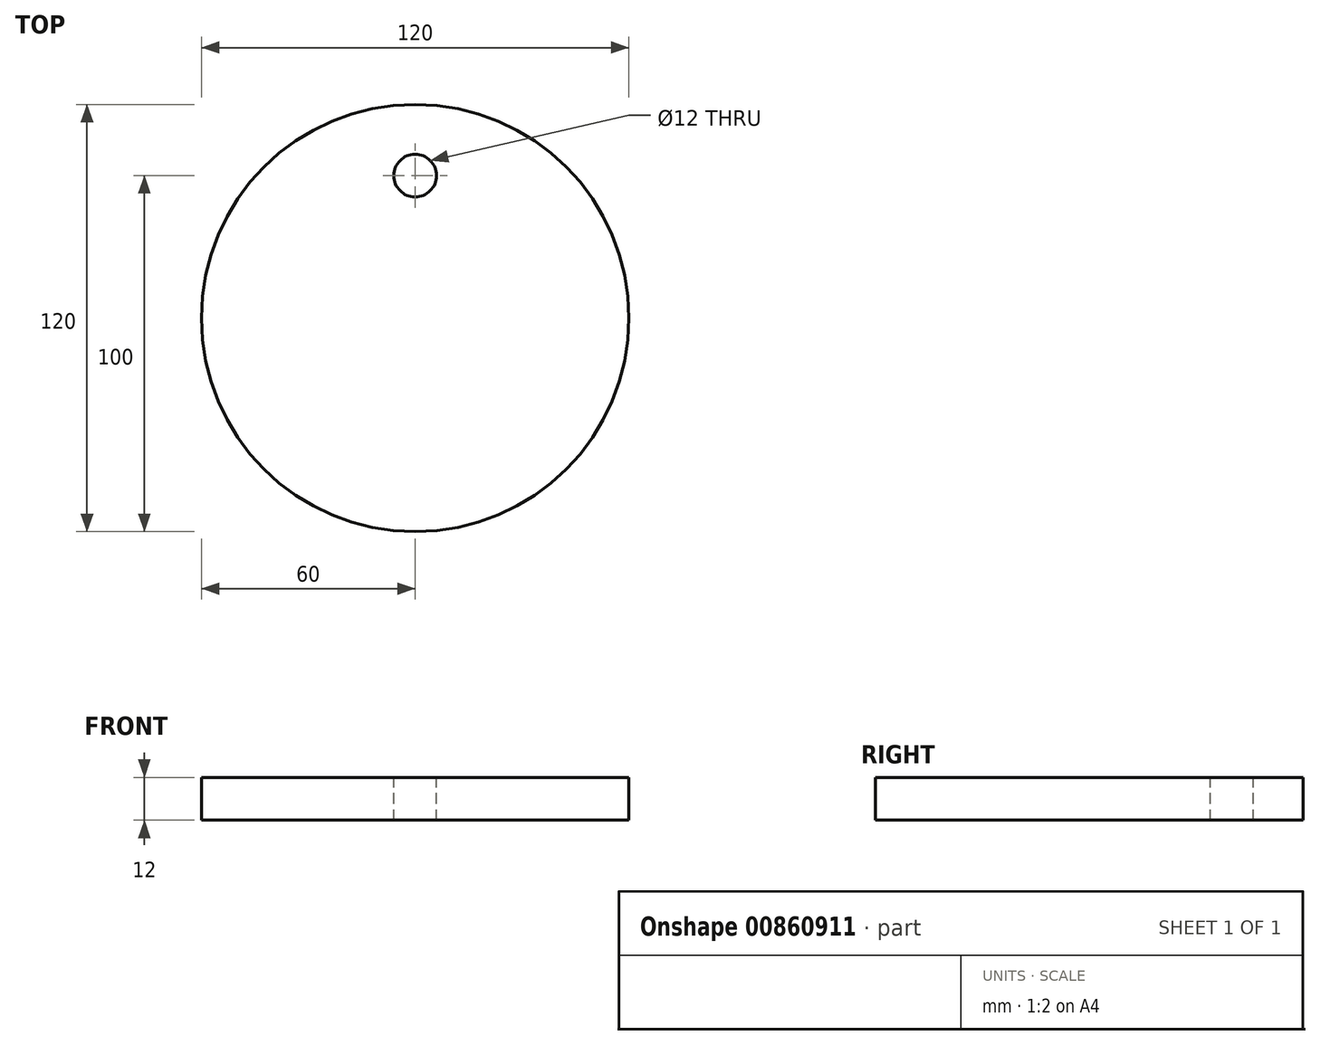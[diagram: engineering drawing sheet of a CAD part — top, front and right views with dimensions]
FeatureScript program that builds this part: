
annotation { "Feature Type Name" : "Feature", "Feature Type Description" : "" }
export const myFeature = defineFeature(function(context is Context, id is Id, definition is map)
    precondition{}
    {
        {
            assignVariable(context, id + "F0", {"name" : "BigCircle", "anyValue" : 120});
        }
        {
            assignVariable(context, id + "F1", {"name" : "Thickness", "anyValue" : getVariable(context, 'BigCircle') / 10});
        }
        {
            var Q0;
            Q0=qCreatedBy(makeId("Top.planeOp"),FACE);
            var sketch = newSketch(context, id + "F2", { "sketchPlane" : qUnion([Q0])});
            skCircle(sketch, "E0", {"center": v(0, 0) * mm, "radius": 60 * mm});
            skSolve(sketch);
        }
        {
            var Q0;
            Q0 = qSketchRegion(id + "F2", true);
            extrude(context, id + "F3", {"entities" : qUnion([Q0]), "depth" : (getVariable(context, 'Thickness')) * mm, "offsetDistance" : 25 * mm});
        }
        {
            var Q0;
            Q0=makeQuery(id+"F3.opExtrude","CAP_FACE",FACE,{"disambiguationData":[OSD([sQuery(id+"F2.wireOp",EDGE,"E0")])],"isStart":false});
            var sketch = newSketch(context, id + "F4", { "sketchPlane" : qUnion([Q0])});
            skCircle(sketch, "E1", {"center": v(0, 0) * mm, "radius": 40 * mm, "construction": true});
            skCircle(sketch, "E2", {"center": v(0, 40) * mm, "radius": 6 * mm});
            skSolve(sketch);
        }
        {
            var Q0;
            Q0 = qSketchRegion(id + "F4", true);
            extrude(context, id + "F5", {"entities" : qUnion([Q0]), "operationType" : NewBodyOperationType.REMOVE, "endBound" : BoundingType.THROUGH_ALL, "oppositeDirection" : true, "depth" : mm, "offsetDistance" : 25 * mm});
        }
    });
